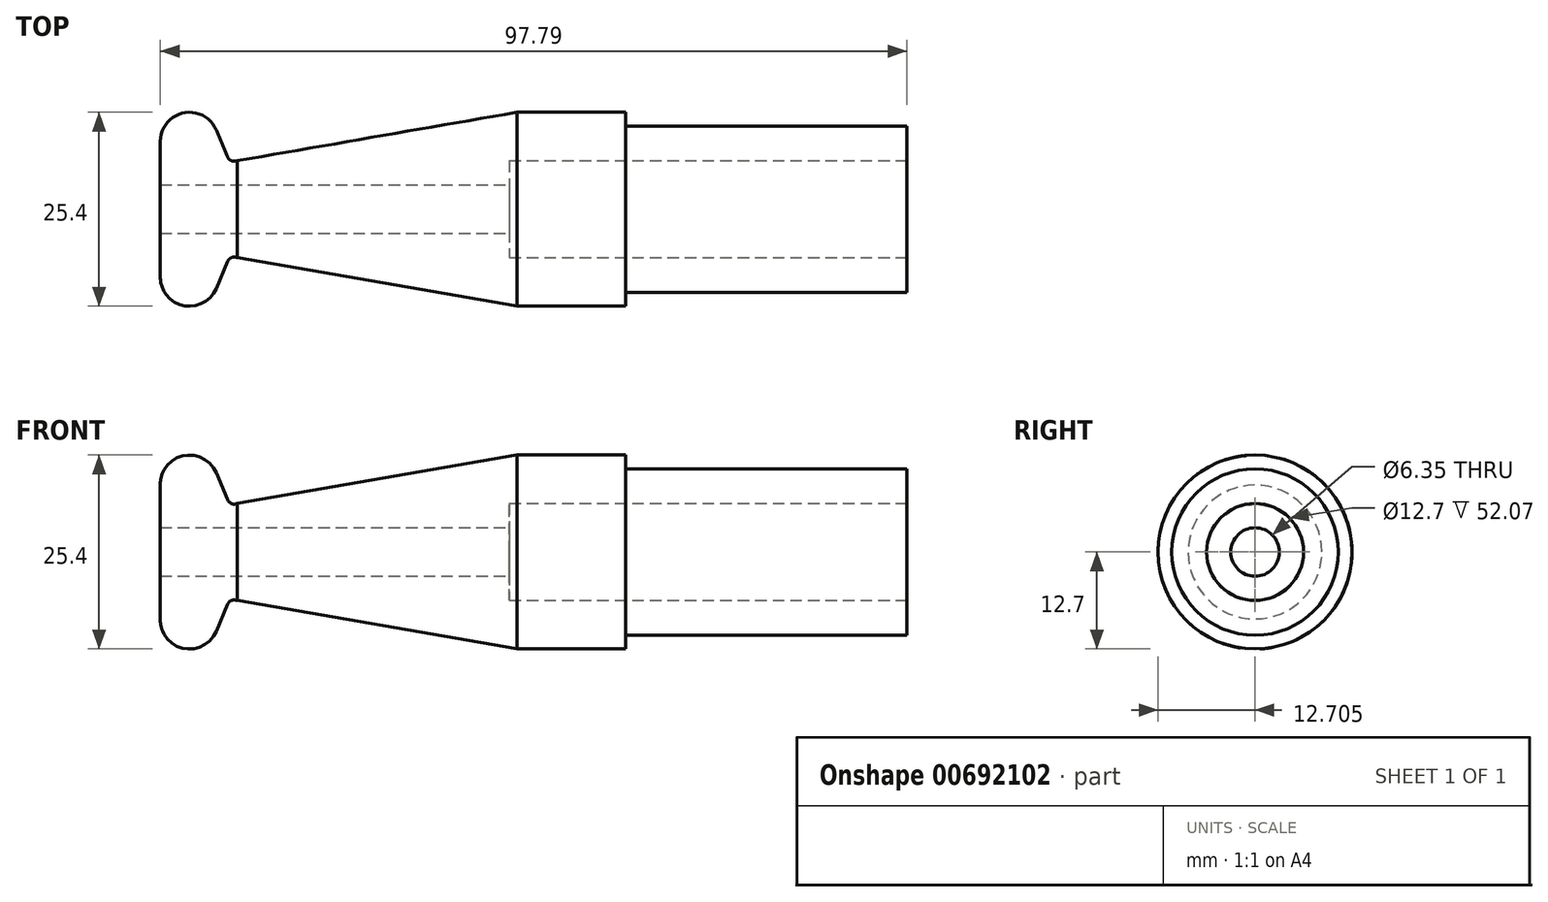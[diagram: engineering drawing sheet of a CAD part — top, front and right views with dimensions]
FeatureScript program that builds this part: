
annotation { "Feature Type Name" : "Feature", "Feature Type Description" : "" }
export const myFeature = defineFeature(function(context is Context, id is Id, definition is map)
    precondition{}
    {
        {
            var Q0;
            Q0=qCreatedBy(makeId("Top.planeOp"),FACE);
            var sketch = newSketch(context, id + "F0", { "sketchPlane" : qUnion([Q0])});
            skLineSegment(sketch, "E0", {"start": v(0, 0) * mm, "end": v(-277.96, 0) * mm});
            skLineSegment(sketch, "E1", {"start": v(-0.62, 44.52) * mm, "end": v(-164.38, 44.52) * mm, "construction": true});
            skLineSegment(sketch, "E2", {"start": v(-93.14, 50.87) * mm, "end": v(-93.14, 47.7) * mm});
            skLineSegment(sketch, "E3", {"start": v(-93.14, 47.7) * mm, "end": v(-126.84, 47.7) * mm});
            skLineSegment(sketch, "E4", {"start": v(-126.84, 47.7) * mm, "end": v(-126.84, 44.75) * mm});
            skLineSegment(sketch, "E5", {"start": v(-41.07, 50.87) * mm, "end": v(-41.07, 55.42) * mm});
            skLineSegment(sketch, "E6", {"start": v(-41.07, 55.42) * mm, "end": v(-77.9, 55.42) * mm});
            skLineSegment(sketch, "E7", {"start": v(-77.9, 55.42) * mm, "end": v(-77.9, 57.22) * mm});
            skLineSegment(sketch, "E8", {"start": v(-77.9, 57.22) * mm, "end": v(-92.12, 57.22) * mm});
            skLineSegment(sketch, "E9", {"start": v(-92.12, 57.22) * mm, "end": v(-128.81, 50.87) * mm});
            skLineSegment(sketch, "E10", {"start": v(-130.06, 51.38) * mm, "end": v(-131.54, 54.9) * mm});
            skLineSegment(sketch, "E11", {"start": v(-126.84, 47.7) * mm, "end": v(-138.86, 47.7) * mm});
            skLineSegment(sketch, "E12", {"start": v(-138.86, 47.7) * mm, "end": v(-138.86, 53.29) * mm});
            skArc(sketch, "E13", {"start": v(-131.54, 54.9) * mm, "mid": v(-135.87, 57.14) * mm, "end": v(-138.86, 53.29) * mm});
            skLineSegment(sketch, "E14", {"start": v(-93.14, 50.87) * mm, "end": v(-41.07, 50.87) * mm});
            skArc(sketch, "E15", {"start": v(-130.06, 51.38) * mm, "mid": v(-129.54, 50.87) * mm, "end": v(-128.81, 50.87) * mm});
            skSolve(sketch);
        }
        {
            var Q0;
            Q0=makeQuery(id+"F0.imprint","IMPRINT",FACE,{"disambiguationData":[TD([[makeQuery(id+"F0.imprint","IMPRINT",EDGE,{"derivedFrom":sQuery(id+"F0.wireOp",EDGE,"E2")}),-1.0]])]});
            var Q1;
            Q1=sQuery(id+"F0.wireOp",EDGE,"E1");
            revolve(context, id + "F1", {"entities" : qUnion([Q0]), "axis" : qUnion([Q1]), "revolveType" : RevolveType.FULL});
        }
    });
